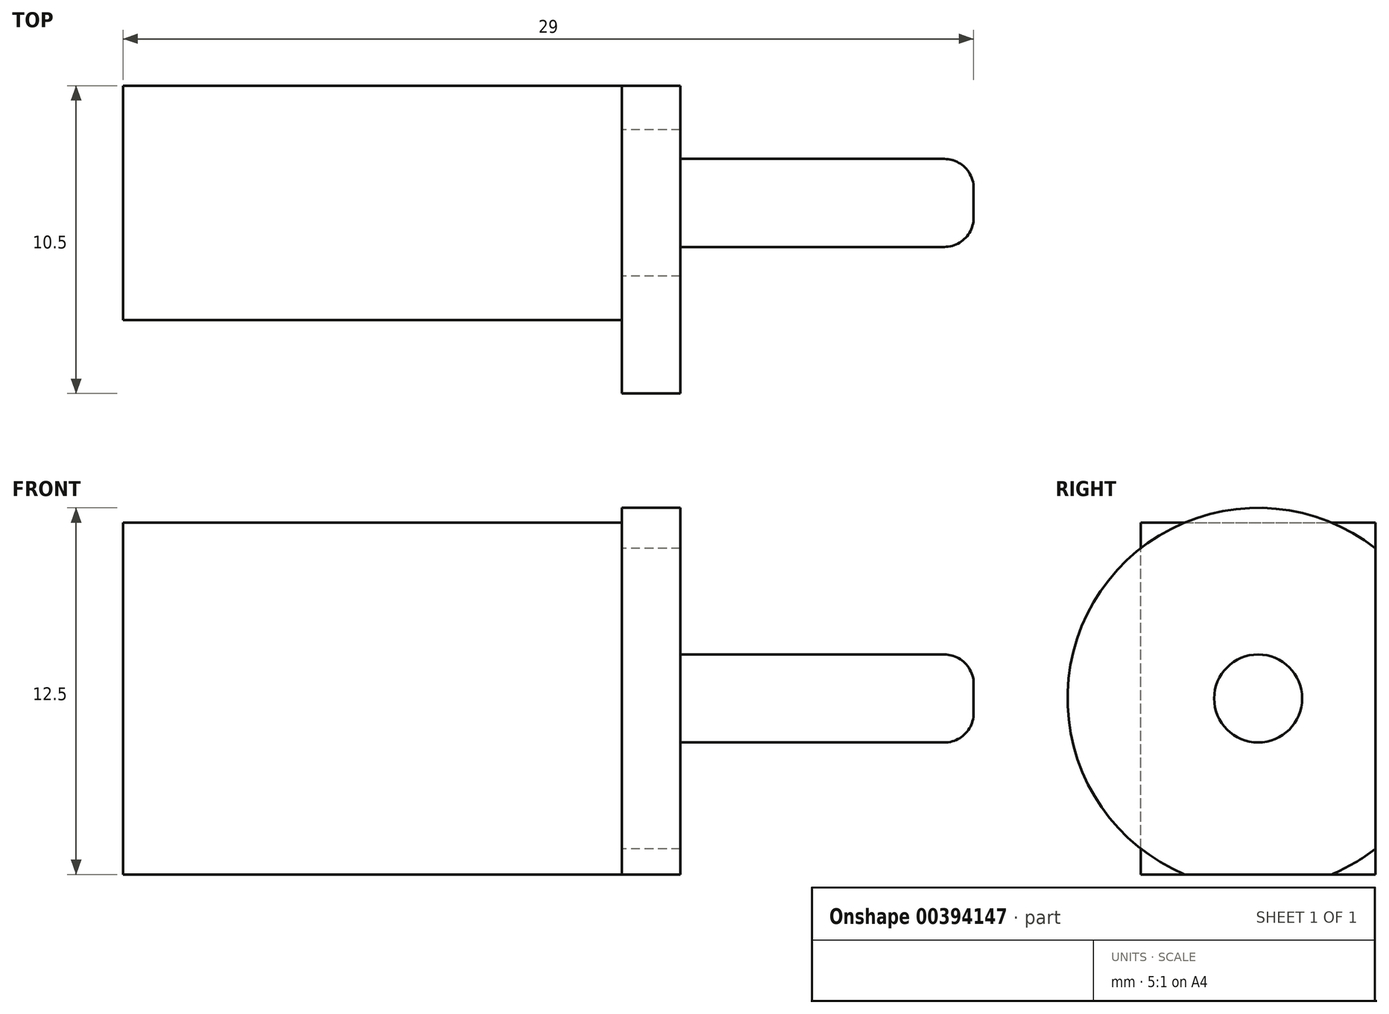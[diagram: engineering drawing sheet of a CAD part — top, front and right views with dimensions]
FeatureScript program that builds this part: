
annotation { "Feature Type Name" : "Feature", "Feature Type Description" : "" }
export const myFeature = defineFeature(function(context is Context, id is Id, definition is map)
    precondition{}
    {
        {
            var Q0;
            Q0=qCreatedBy(makeId("Front.planeOp"),FACE);
            var sketch = newSketch(context, id + "F0", { "sketchPlane" : qUnion([Q0])});
            skLineSegment(sketch, "E0.bottom", {"start": v(8.5, -6) * mm, "end": v(-8.5, -6) * mm});
            skLineSegment(sketch, "E0.top", {"start": v(8.5, 6) * mm, "end": v(-8.5, 6) * mm});
            skLineSegment(sketch, "E0.left", {"start": v(8.5, -6) * mm, "end": v(8.5, 6) * mm});
            skLineSegment(sketch, "E0.right", {"start": v(-8.5, -6) * mm, "end": v(-8.5, 6) * mm});
            skPoint(sketch, "E0.middle", {"position": v(0, 0) * mm});
            skSolve(sketch);
        }
        {
            var Q0;
            Q0=makeQuery(id+"F0.imprint","IMPRINT",FACE,{"disambiguationData":[TD([[makeQuery(id+"F0.imprint","IMPRINT",EDGE,{"derivedFrom":sQuery(id+"F0.wireOp",EDGE,"E0.bottom")}),-1.0]])]});
            extrude(context, id + "F1", {"entities" : qUnion([Q0]), "depth" : 8 * mm});
        }
        {
            var Q0;
            Q0=makeQuery(id+"F1.opExtrude","SWEPT_FACE",FACE,{"disambiguationData":[OSD([sQuery(id+"F0.wireOp",EDGE,"E0.left")])]});
            var sketch = newSketch(context, id + "F2", { "sketchPlane" : qUnion([Q0])});
            skCircle(sketch, "E1", {"center": v(-4, 0) * mm, "radius": 6.5 * mm});
            skPoint(sketch, "E1.centerSnap0", {"position": v(-4, 6) * mm});
            skPoint(sketch, "E1.centerSnap1", {"position": v(-8, 0) * mm});
            skSolve(sketch);
        }
        {
            var Q0;
            Q0=makeQuery(id+"F2.imprint","IMPRINT",FACE,{"disambiguationData":[TD([[makeQuery(id+"F2.imprint","IMPRINT",EDGE,{"derivedFrom":sQuery(id+"F2.wireOp",EDGE,"E1")}),1.0]])]});
            var Q1;
            {var subQ0=sQuery(id+"F2.wireOp",EDGE,"E1");var subQ1=makeQuery(id+"F1.opExtrude","CAP_EDGE",EDGE,{"disambiguationData":[OSD([sQuery(id+"F0.wireOp",EDGE,"E0.left")])],"isStart":true});var subQ2=makeQuery(id+"F2.imprint","INTERSECT",VERTEX,{"disambiguationData":[OD(0.0)],"derivedFrom":[subQ1,subQ0]});Q1=makeQuery(id+"F2.imprint","IMPRINT",FACE,{"disambiguationData":[TD([[makeQuery(id+"F2.imprint","IMPRINT",EDGE,{"disambiguationData":[TD([[subQ2,1.0]])],"derivedFrom":subQ0}),1.0]])]});}
            var Q2;
            {var subQ0=sQuery(id+"F2.wireOp",EDGE,"E1");var subQ1=makeQuery(id+"F1.opExtrude","SWEPT_EDGE",EDGE,{"disambiguationData":[OSD([sQuery(id+"F0.wireOp",EDGE,"E0.top"),sQuery(id+"F0.wireOp",EDGE,"E0.left")])]});var subQ2=makeQuery(id+"F2.imprint","INTERSECT",VERTEX,{"disambiguationData":[OD(0.0)],"derivedFrom":[subQ1,subQ0]});Q2=makeQuery(id+"F2.imprint","IMPRINT",FACE,{"disambiguationData":[TD([[makeQuery(id+"F2.imprint","IMPRINT",EDGE,{"disambiguationData":[TD([[subQ2,-1.0]])],"derivedFrom":subQ0}),1.0]])]});}
            var Q3;
            {var subQ0=sQuery(id+"F2.wireOp",EDGE,"E1");var subQ1=makeQuery(id+"F1.opExtrude","CAP_EDGE",EDGE,{"disambiguationData":[OSD([sQuery(id+"F0.wireOp",EDGE,"E0.left")])],"isStart":false});var subQ2=makeQuery(id+"F2.imprint","INTERSECT",VERTEX,{"disambiguationData":[OD(0.0)],"derivedFrom":[subQ1,subQ0]});Q3=makeQuery(id+"F2.imprint","IMPRINT",FACE,{"disambiguationData":[TD([[makeQuery(id+"F2.imprint","IMPRINT",EDGE,{"disambiguationData":[TD([[subQ2,-1.0]])],"derivedFrom":subQ0}),1.0]])]});}
            var Q4;
            {var subQ0=sQuery(id+"F2.wireOp",EDGE,"E1");var subQ1=makeQuery(id+"F1.opExtrude","SWEPT_EDGE",EDGE,{"disambiguationData":[OSD([sQuery(id+"F0.wireOp",EDGE,"E0.bottom"),sQuery(id+"F0.wireOp",EDGE,"E0.left")])]});var subQ2=makeQuery(id+"F2.imprint","INTERSECT",VERTEX,{"disambiguationData":[OD(0.0)],"derivedFrom":[subQ1,subQ0]});Q4=makeQuery(id+"F2.imprint","IMPRINT",FACE,{"disambiguationData":[TD([[makeQuery(id+"F2.imprint","IMPRINT",EDGE,{"disambiguationData":[TD([[subQ2,-1.0]])],"derivedFrom":subQ0}),1.0]])]});}
            extrude(context, id + "F3", {"entities" : qUnion([Q0, Q1, Q2, Q3, Q4]), "depth" : 2 * mm});
        }
        {
            var Q0;
            Q0=makeQuery(id+"F3.opExtrude","CAP_FACE",FACE,{"disambiguationData":[OSD([sQuery(id+"F2.wireOp",EDGE,"E1")])],"isStart":false});
            var sketch = newSketch(context, id + "F4", { "sketchPlane" : qUnion([Q0])});
            skCircle(sketch, "E2.0.0", {"center": v(-4, 0) * mm, "radius": 6.5 * mm});
            skCircle(sketch, "E3", {"center": v(-4, 0) * mm, "radius": 1.5 * mm});
            skSolve(sketch);
        }
        {
            var Q0;
            Q0=makeQuery(id+"F4.imprint","IMPRINT",FACE,{"disambiguationData":[TD([[makeQuery(id+"F4.imprint","IMPRINT",EDGE,{"derivedFrom":sQuery(id+"F4.wireOp",EDGE,"E3")}),1.0]])]});
            var Q1;
            Q1=sQuery(id+"F4.wireOp",EDGE,"E3");
            extrude(context, id + "F5", {"entities" : qUnion([Q0]), "surfaceEntities" : qUnion([Q1]), "depth" : 10 * mm});
        }
        {
            var Q0;
            Q0=makeQuery(id+"F5.opExtrude","CAP_EDGE",EDGE,{"disambiguationData":[OSD([sQuery(id+"F4.wireOp",EDGE,"E3")])],"isStart":false});
            fillet(context, id + "F6", {"entities" : qUnion([Q0]), "radius" : 1 * mm, "tangentPropagation" : true, "allowEdgeOverflow" : false});
        }
    });
